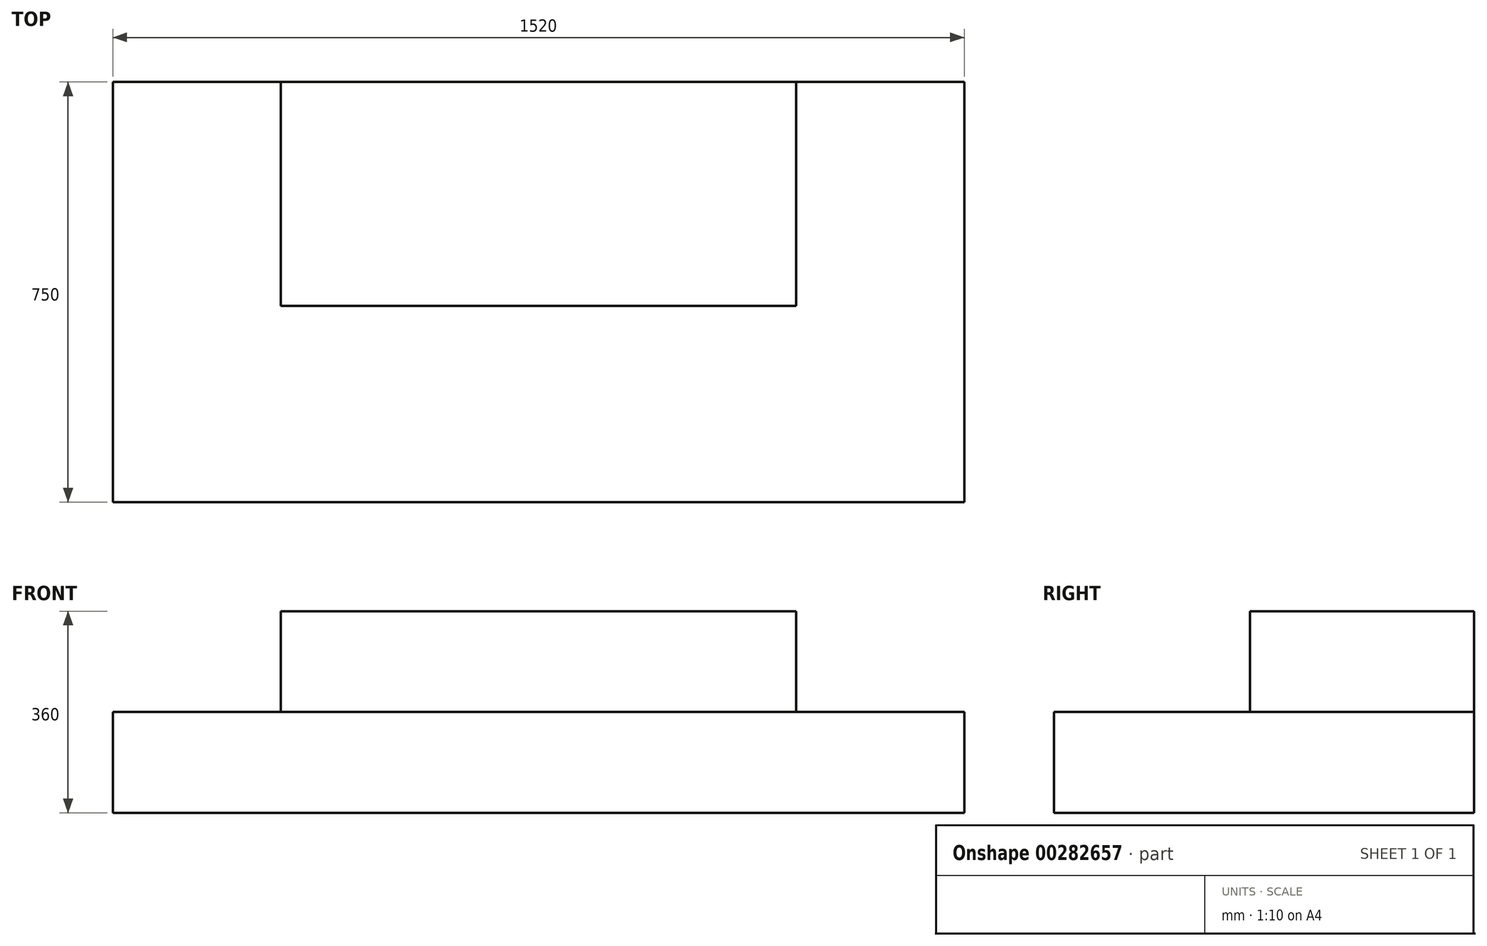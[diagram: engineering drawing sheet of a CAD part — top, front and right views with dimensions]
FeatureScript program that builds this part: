
annotation { "Feature Type Name" : "Feature", "Feature Type Description" : "" }
export const myFeature = defineFeature(function(context is Context, id is Id, definition is map)
    precondition{}
    {
        {
            var Q0;
            Q0=qCreatedBy(makeId("Top.planeOp"),FACE);
            var sketch = newSketch(context, id + "F0", { "sketchPlane" : qUnion([Q0])});
            skLineSegment(sketch, "E0.bottom", {"start": v(-760, -375) * mm, "end": v(760, -375) * mm});
            skLineSegment(sketch, "E0.top", {"start": v(-760, 375) * mm, "end": v(760, 375) * mm});
            skLineSegment(sketch, "E0.left", {"start": v(-760, -375) * mm, "end": v(-760, 375) * mm});
            skLineSegment(sketch, "E0.right", {"start": v(760, -375) * mm, "end": v(760, 375) * mm});
            skPoint(sketch, "E0.middle", {"position": v(0, 0) * mm});
            skSolve(sketch);
        }
        {
            var Q0;
            Q0 = qSketchRegion(id + "F0", true);
            extrude(context, id + "F1", {"entities" : qUnion([Q0]), "depth" : 180 * mm, "offsetDistance" : 25 * mm});
        }
        {
            var Q0;
            Q0=makeQuery(id+"F1.opExtrude","CAP_FACE",FACE,{"disambiguationData":[OSD([sQuery(id+"F0.wireOp",EDGE,"E0.bottom"),sQuery(id+"F0.wireOp",EDGE,"E0.top"),sQuery(id+"F0.wireOp",EDGE,"E0.left"),sQuery(id+"F0.wireOp",EDGE,"E0.right")])],"isStart":false});
            var sketch = newSketch(context, id + "F2", { "sketchPlane" : qUnion([Q0])});
            skLineSegment(sketch, "E1.bottom", {"start": v(-460, 375) * mm, "end": v(460, 375) * mm});
            skLineSegment(sketch, "E1.top", {"start": v(-460, -25) * mm, "end": v(460, -25) * mm});
            skLineSegment(sketch, "E1.left", {"start": v(-460, 375) * mm, "end": v(-460, -25) * mm});
            skLineSegment(sketch, "E1.right", {"start": v(460, 375) * mm, "end": v(460, -25) * mm});
            skSolve(sketch);
        }
        {
            var Q0;
            Q0 = qSketchRegion(id + "F2", true);
            extrude(context, id + "F3", {"entities" : qUnion([Q0]), "operationType" : NewBodyOperationType.ADD, "depth" : 180 * mm, "offsetDistance" : 25 * mm});
        }
    });
